# Revit family: IQ8Wireless universal interface
name_source: partatom
category: Fire Alarm Devices
revit_build: Autodesk Revit 2014 (Build: 20130308_1515(x64)
units: mm (PartAtom-declared; Revit-internal decimal feet)

## types (2) — shared parameters
Fire Alarm Device 01 = IQ8 MCP Large : MCP Large
Manufacturer = Esser by Honeywell
URL = http://www.esser-systems.com
b1 = 20 mm  [stored 0.0656168 ft]
content_date_modified = 16.06.2015
content_version = 1.0
h1 = 135 mm  [stored 0.442913 ft]
l1 = 135 mm  [stored 0.442913 ft]

## per-type parameters (varying)
| type | Model | article number | material |
| IQ8Wireless universal interface red | IQ8Wireless universal interface w/o cover, red | 805601.1 | Red |
| IQ8Wireless universal interface white | IQ8Wireless universal interface w/o cover, white | 805602.1 | White |

note: [stored X ft] marks values corroborated as IEEE doubles in the binary element streams (Revit-internal decimal feet)

## geometry (parser evidence)
native form markers: Sweep x6
no freeform markers — native parametric forms only
